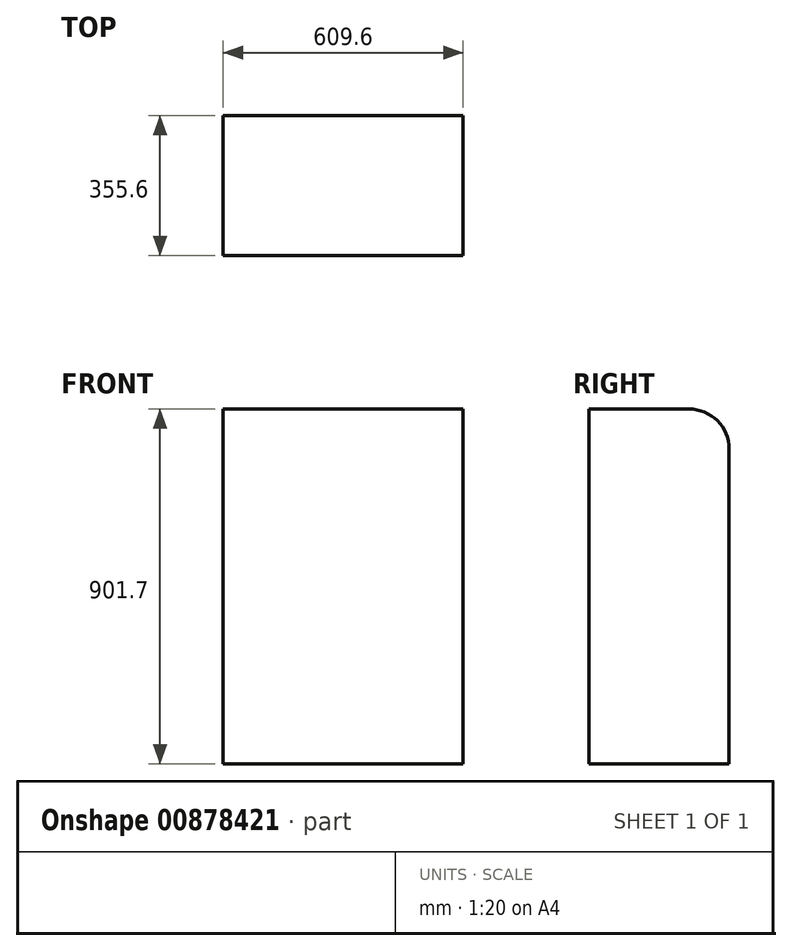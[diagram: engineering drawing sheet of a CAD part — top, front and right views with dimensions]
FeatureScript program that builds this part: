
annotation { "Feature Type Name" : "Feature", "Feature Type Description" : "" }
export const myFeature = defineFeature(function(context is Context, id is Id, definition is map)
    precondition{}
    {
        {
            var Q0;
            Q0=qCreatedBy(makeId("Right.planeOp"),FACE);
            var sketch = newSketch(context, id + "F0", { "sketchPlane" : qUnion([Q0])});
            skLineSegment(sketch, "E0.bottom", {"start": v(0, 0) * mm, "end": v(-355.6, 0) * mm});
            skLineSegment(sketch, "E0.top", {"start": v(-101.6, 901.7) * mm, "end": v(-355.6, 901.7) * mm});
            skLineSegment(sketch, "E0.left", {"start": v(0, 0) * mm, "end": v(0, 800.1) * mm});
            skLineSegment(sketch, "E0.right", {"start": v(-355.6, 0) * mm, "end": v(-355.6, 901.7) * mm});
            skPoint(sketch, "E1.visualSharp", {"position": v(0, 901.7) * mm});
            skArc(sketch, "E1.filletArc", {"start": v(0, 800.1) * mm, "mid": v(-29.76, 871.94) * mm, "end": v(-101.6, 901.7) * mm});
            skSolve(sketch);
        }
        {
            var Q0;
            Q0=makeQuery(id+"F0.imprint","IMPRINT",FACE,{"disambiguationData":[TD([[makeQuery(id+"F0.imprint","IMPRINT",EDGE,{"derivedFrom":sQuery(id+"F0.wireOp",EDGE,"E0.bottom")}),-1.0]])]});
            extrude(context, id + "F1", {"entities" : qUnion([Q0]), "depth" : 609.6 * mm, "offsetDistance" : 25.4 * mm});
        }
    });
